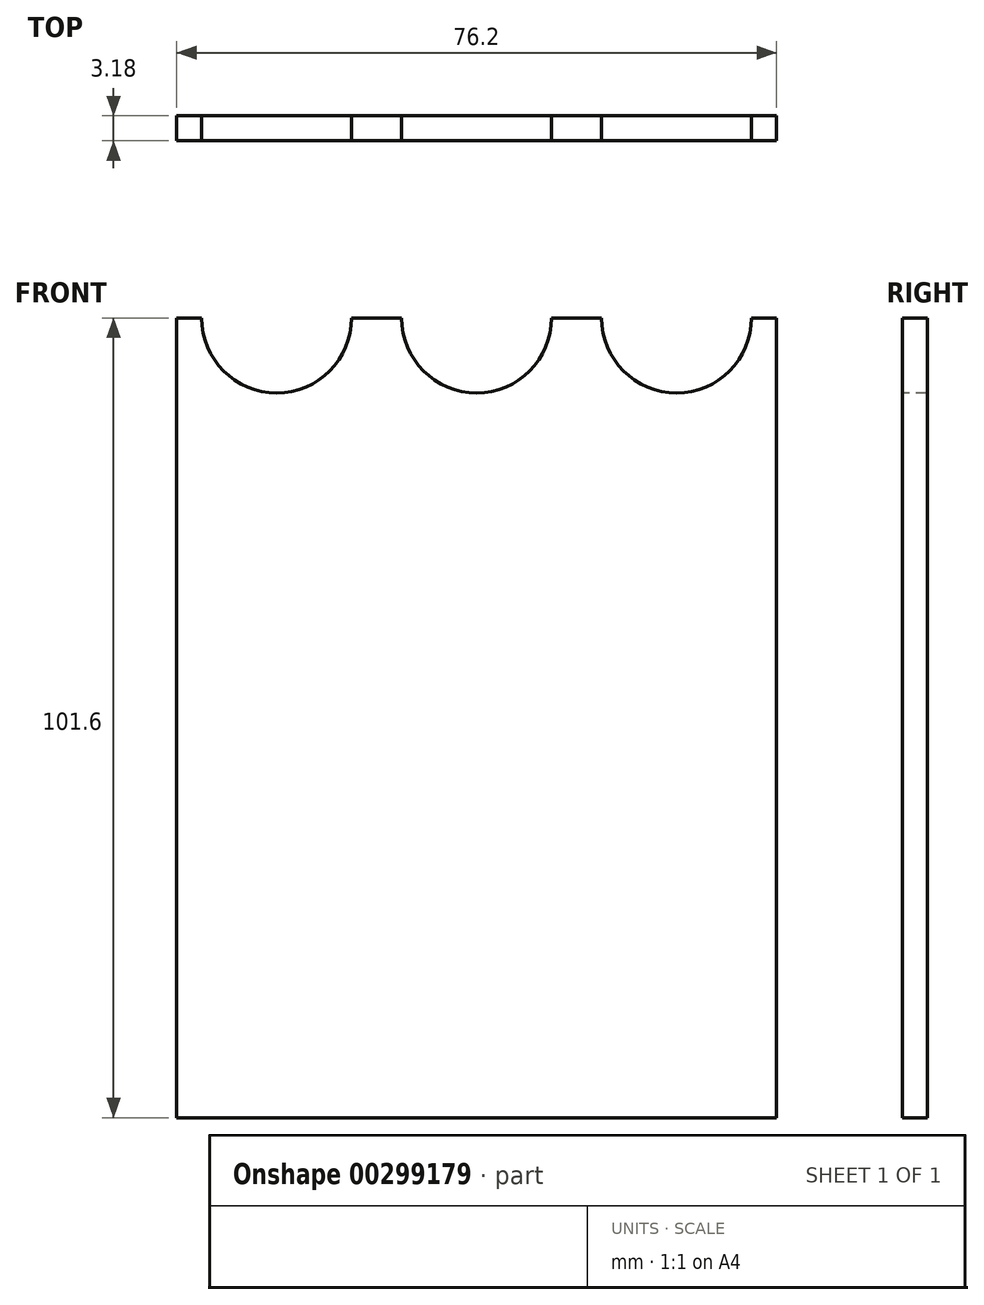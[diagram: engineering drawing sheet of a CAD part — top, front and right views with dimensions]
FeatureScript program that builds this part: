
annotation { "Feature Type Name" : "Feature", "Feature Type Description" : "" }
export const myFeature = defineFeature(function(context is Context, id is Id, definition is map)
    precondition{}
    {
        {
            var Q0;
            Q0=qCreatedBy(makeId("Front.planeOp"),FACE);
            var sketch = newSketch(context, id + "F0", { "sketchPlane" : qUnion([Q0])});
            skLineSegment(sketch, "E0.bottom", {"start": v(38.1, 50.8) * mm, "end": v(-38.1, 50.8) * mm});
            skLineSegment(sketch, "E0.top", {"start": v(38.1, -50.8) * mm, "end": v(-38.1, -50.8) * mm});
            skLineSegment(sketch, "E0.left", {"start": v(38.1, 50.8) * mm, "end": v(38.1, -50.8) * mm});
            skLineSegment(sketch, "E0.right", {"start": v(-38.1, 50.8) * mm, "end": v(-38.1, -50.8) * mm});
            skPoint(sketch, "E0.middle", {"position": v(0, 0) * mm});
            skSolve(sketch);
        }
        {
            var Q0;
            Q0 = qSketchRegion(id + "F0", true);
            extrude(context, id + "F1", {"entities" : qUnion([Q0]), "endBound" : BoundingType.SYMMETRIC, "depth" : 3.17 * mm});
        }
        {
            var Q0;
            Q0=makeQuery(id+"F1.opExtrude","CAP_FACE",FACE,{"disambiguationData":[OSD([sQuery(id+"F0.wireOp",EDGE,"E0.bottom"),sQuery(id+"F0.wireOp",EDGE,"E0.top"),sQuery(id+"F0.wireOp",EDGE,"E0.left"),sQuery(id+"F0.wireOp",EDGE,"E0.right")])],"isStart":false});
            var sketch = newSketch(context, id + "F2", { "sketchPlane" : qUnion([Q0])});
            skArc(sketch, "E1", {"start": v(-25.56, 41.28) * mm, "mid": v(-32.2, 44.12) * mm, "end": v(-34.93, 50.8) * mm});
            skArc(sketch, "E2", {"start": v(-25.56, 41.28) * mm, "mid": v(-18.72, 44) * mm, "end": v(-15.88, 50.8) * mm});
            skArc(sketch, "E3", {"start": v(-0.17, 41.28) * mm, "mid": v(6.67, 44) * mm, "end": v(9.52, 50.8) * mm});
            skArc(sketch, "E4", {"start": v(-0.17, 41.28) * mm, "mid": v(-6.8, 44.13) * mm, "end": v(-9.53, 50.8) * mm});
            skArc(sketch, "E5", {"start": v(24.98, 41.28) * mm, "mid": v(31.99, 43.92) * mm, "end": v(34.92, 50.8) * mm});
            skArc(sketch, "E6", {"start": v(24.98, 41.28) * mm, "mid": v(18.52, 44.21) * mm, "end": v(15.87, 50.8) * mm});
            skLineSegment(sketch, "E7", {"start": v(-34.93, 50.8) * mm, "end": v(-15.88, 50.8) * mm});
            skLineSegment(sketch, "E8", {"start": v(-9.53, 50.8) * mm, "end": v(9.52, 50.8) * mm});
            skLineSegment(sketch, "E9", {"start": v(15.87, 50.8) * mm, "end": v(34.92, 50.8) * mm});
            skSolve(sketch);
        }
        {
            var Q0;
            Q0 = qSketchRegion(id + "F2", true);
            extrude(context, id + "F3", {"entities" : qUnion([Q0]), "operationType" : NewBodyOperationType.REMOVE, "endBound" : BoundingType.THROUGH_ALL, "oppositeDirection" : true, "depth" : 25.4 * mm});
        }
    });
